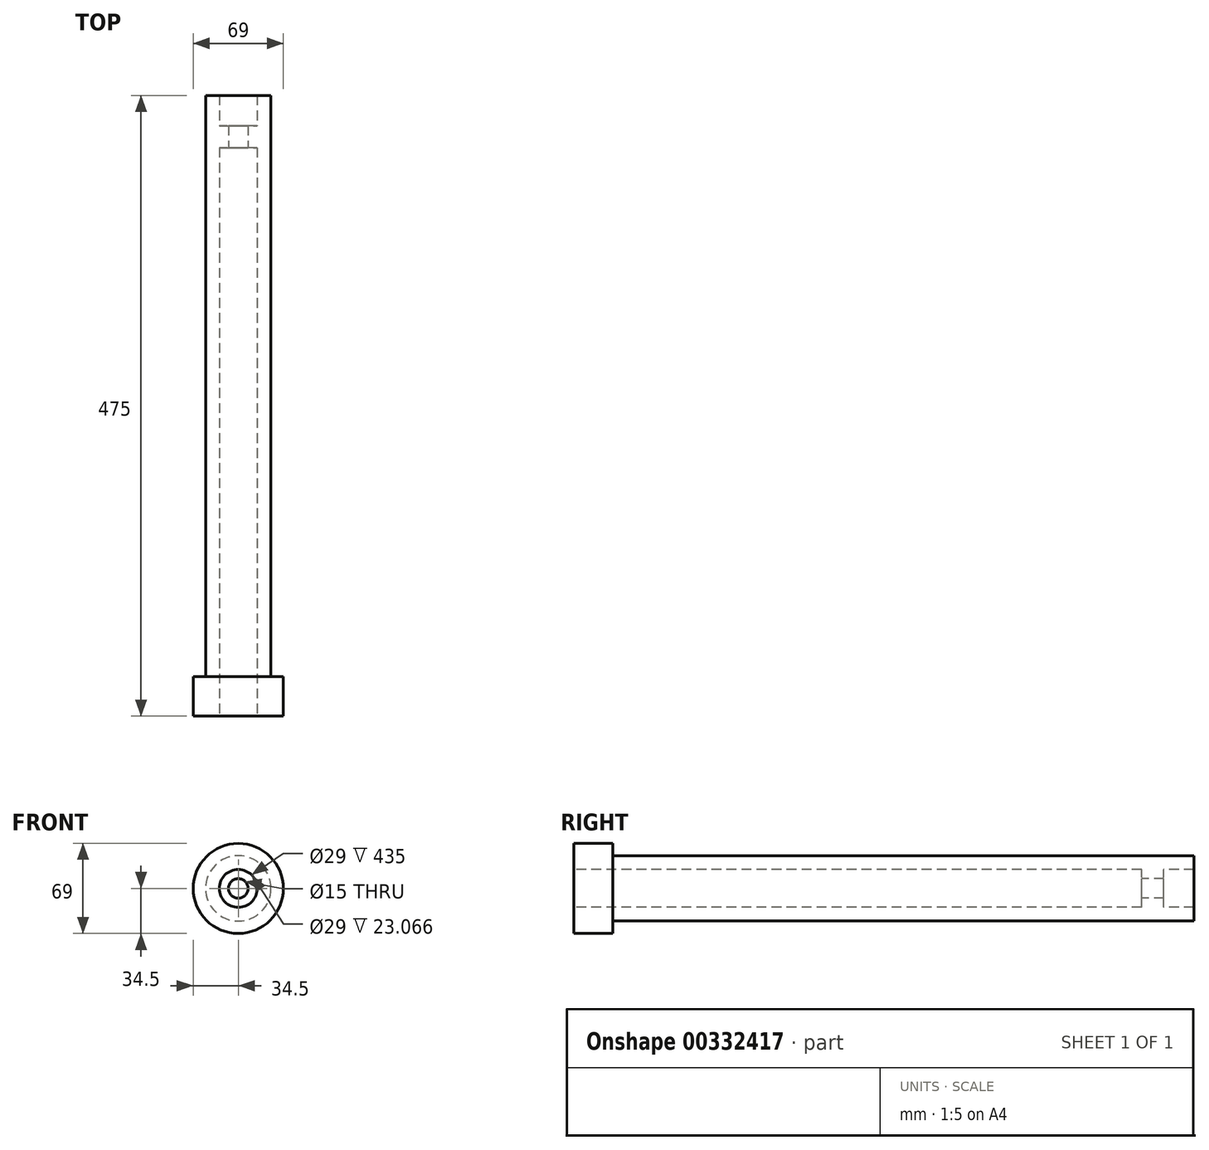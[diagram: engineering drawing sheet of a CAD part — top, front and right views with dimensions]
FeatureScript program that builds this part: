
annotation { "Feature Type Name" : "Feature", "Feature Type Description" : "" }
export const myFeature = defineFeature(function(context is Context, id is Id, definition is map)
    precondition{}
    {
        {
            var Q0;
            Q0=qCreatedBy(makeId("Right.planeOp"),FACE);
            var sketch = newSketch(context, id + "F0", { "sketchPlane" : qUnion([Q0])});
            skLineSegment(sketch, "E0.bottom", {"start": v(-81.02, 34.5) * mm, "end": v(-51.02, 34.5) * mm});
            skLineSegment(sketch, "E0.top", {"start": v(-81.02, 14.5) * mm, "end": v(-51.02, 14.5) * mm});
            skLineSegment(sketch, "E0.left", {"start": v(-81.02, 34.5) * mm, "end": v(-81.02, 14.5) * mm});
            skLineSegment(sketch, "E0.right", {"start": v(-51.02, 34.5) * mm, "end": v(-51.02, 14.5) * mm});
            skPoint(sketch, "E1.oppositeSnap0", {"position": v(-40.36, 27.63) * mm});
            skLineSegment(sketch, "E2.bottom", {"start": v(-51.02, 14.5) * mm, "end": v(393.98, 14.5) * mm});
            skLineSegment(sketch, "E2.top", {"start": v(-51.02, 25) * mm, "end": v(393.98, 25) * mm});
            skLineSegment(sketch, "E2.left", {"start": v(-51.02, 14.5) * mm, "end": v(-51.02, 25) * mm});
            skLineSegment(sketch, "E2.right", {"start": v(393.98, 14.5) * mm, "end": v(393.98, 25) * mm});
            skLineSegment(sketch, "E3.bottom", {"start": v(370.92, 14.5) * mm, "end": v(353.98, 14.5) * mm});
            skLineSegment(sketch, "E3.top", {"start": v(370.92, 7.5) * mm, "end": v(353.98, 7.5) * mm});
            skLineSegment(sketch, "E3.left", {"start": v(370.92, 14.5) * mm, "end": v(370.92, 7.5) * mm});
            skLineSegment(sketch, "E3.right", {"start": v(353.98, 14.5) * mm, "end": v(353.98, 7.5) * mm});
            skLineSegment(sketch, "E4", {"start": v(0, 0) * mm, "end": v(214.3, 0) * mm, "construction": true});
            skSolve(sketch);
        }
        {
            var Q0;
            {var subQ6=sQuery(id+"F0.wireOp",EDGE,"E2.top");Q0=makeQuery(id+"F0.imprint","IMPRINT",FACE,{"disambiguationData":[TD([[makeQuery(id+"F0.imprint","IMPRINT",EDGE,{"derivedFrom":subQ6}),-1.0]])]});}
            var Q1;
            Q1=makeQuery(id+"F0.imprint","IMPRINT",FACE,{"disambiguationData":[TD([[makeQuery(id+"F0.imprint","IMPRINT",EDGE,{"derivedFrom":sQuery(id+"F0.wireOp",EDGE,"E3.top")}),-1.0]])]});
            var Q2;
            {var subQ3=sQuery(id+"F0.wireOp",EDGE,"E0.bottom");Q2=makeQuery(id+"F0.imprint","IMPRINT",FACE,{"disambiguationData":[TD([[makeQuery(id+"F0.imprint","IMPRINT",EDGE,{"derivedFrom":subQ3}),-1.0]])]});}
            var Q3;
            Q3=sQuery(id+"F0.wireOp",EDGE,"E4");
            revolve(context, id + "F1", {"entities" : qUnion([Q0, Q1, Q2]), "axis" : qUnion([Q3]), "revolveType" : RevolveType.FULL});
        }
    });
